# Revit family: ledspotra-selena-e_5w-930-55d-wh_541003589600
name_source: partatom
category: Lighting Fixtures
units: mm (PartAtom-declared; Revit-internal decimal feet)

## family parameters
Cut with Voids When Loaded = No
Host = Face
Light Source = No
Part Type = Normal
Room Calculation Point = No
Round Connector Dimension = Use Diameter
Shared = No

## types (1)
- LEDSpotRA-Selena-E 5W-930-55D-WH (1 x LED, 400 lm, 3000)
    Apparent Load = 5 VA
    Approval mark = CE
    CIE Flux Codes = 88 99 100 100 100
    Color Rendering = 90
    Color Temperature = 3000
    Control Gear = Electronic ballast
    Default Elevation = 1800 mm
    Description = Stylish and compact surface mounted spot. Clean “twist-and-lock” mounting system. High quality full metal body. Standard CRI 90.
    Frequency = 60 Hz
    Height = 0 mm  [stored 0 ft]
    Lamp = 1 x LED
    Lamp Light Flux = 400 lm
    Lamp count = 1
    Length = 55 mm
    Luminous efficacy = 80 lm/W
    Manufacturer = OPPLE
    ModVariant = No
    Model = 541003589600
    Mounting Place = Ceiling, Pole
    Mounting Type = Surface mounted
    Number of Poles = 1
    OnlyDefault = Yes
    Power Factor = 1
    Product Name = LEDSpotRA-Selena-E 5W-930-55D-WH
    ProductGroupID = 440
    Protection Class = Protection class II
    Protection Degree = IP 20
    RLX_Detail_Level = 1
    RlxData = <blob elided: 124361 chars, md5=ef18121b>
    Socket = socket
    Standby Power = 0 W
    System Light Flux = 400 lm
    System Power = 5 W
    Type Comments = Product without accessories
    Type Image = web_selena_ra-5w-wh.jpg
    URL = http://relux.com
    VarID = ---
    Voltage = 230 V
    Voltage Range = 220-240 V
    Weight = 0.00 kg
    Width = 55 mm

note: [stored X ft] marks values corroborated as IEEE doubles in the binary element streams (Revit-internal decimal feet)

## geometry (parser evidence)
native form markers: Blend x4, Sweep x13
no freeform markers — native parametric forms only
